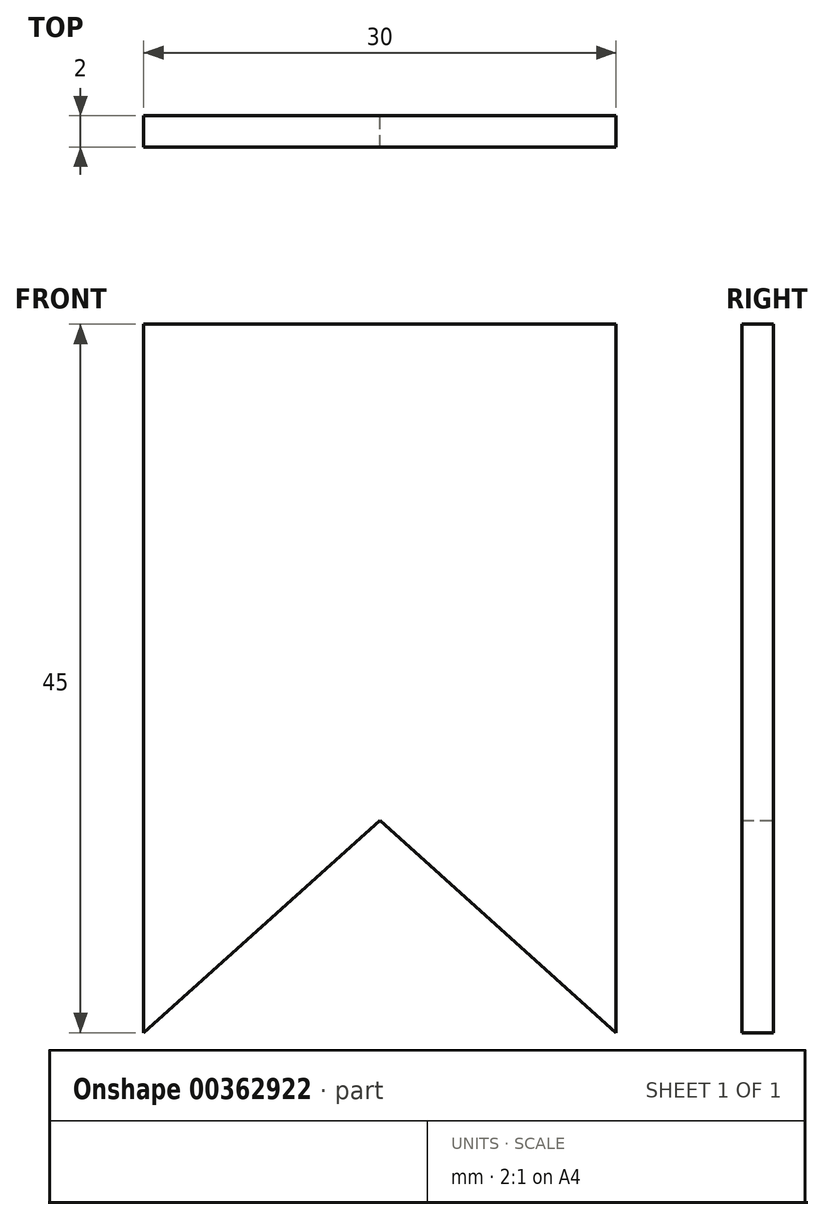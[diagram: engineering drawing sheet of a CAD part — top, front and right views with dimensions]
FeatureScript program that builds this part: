
annotation { "Feature Type Name" : "Feature", "Feature Type Description" : "" }
export const myFeature = defineFeature(function(context is Context, id is Id, definition is map)
    precondition{}
    {
        {
            var Q0;
            Q0=qCreatedBy(makeId("Front.planeOp"),FACE);
            var sketch = newSketch(context, id + "F0", { "sketchPlane" : qUnion([Q0])});
            skLineSegment(sketch, "E0.top", {"start": v(15, 22.5) * mm, "end": v(-15, 22.5) * mm});
            skLineSegment(sketch, "E0.left", {"start": v(15, -22.5) * mm, "end": v(15, 22.5) * mm});
            skLineSegment(sketch, "E0.right", {"start": v(-15, -22.5) * mm, "end": v(-15, 22.5) * mm});
            skPoint(sketch, "E0.middle", {"position": v(0, 0) * mm});
            skLineSegment(sketch, "E1", {"start": v(0, -9.02) * mm, "end": v(-15, -22.5) * mm});
            skLineSegment(sketch, "E2", {"start": v(0, -9.02) * mm, "end": v(15, -22.5) * mm});
            skSolve(sketch);
        }
        {
            var Q0;
            Q0=makeQuery(id+"F0.imprint","IMPRINT",FACE,{"disambiguationData":[TD([[makeQuery(id+"F0.imprint","IMPRINT",EDGE,{"derivedFrom":sQuery(id+"F0.wireOp",EDGE,"E0.top")}),1.0]])]});
            extrude(context, id + "F1", {"entities" : qUnion([Q0]), "depth" : 2 * mm});
        }
    });
